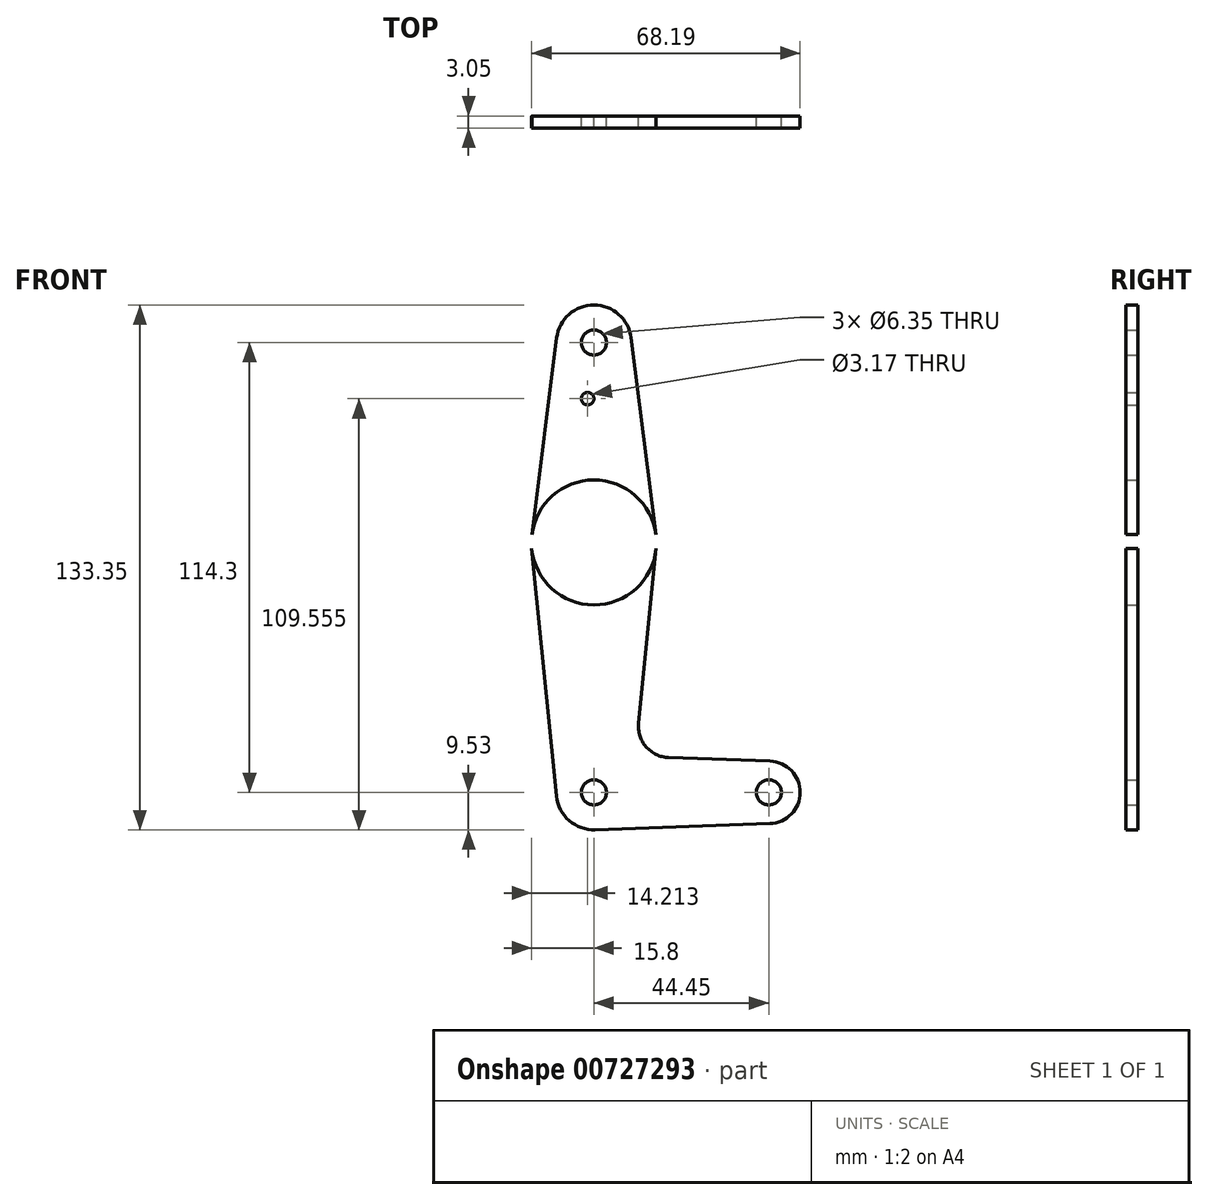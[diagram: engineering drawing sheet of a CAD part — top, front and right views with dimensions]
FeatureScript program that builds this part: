
annotation { "Feature Type Name" : "Feature", "Feature Type Description" : "" }
export const myFeature = defineFeature(function(context is Context, id is Id, definition is map)
    precondition{}
    {
        {
            var Q0;
            Q0=qCreatedBy(makeId("Front.planeOp"),FACE);
            var sketch = newSketch(context, id + "F0", { "sketchPlane" : qUnion([Q0])});
            skLineSegment(sketch, "E0", {"start": v(0, 0) * mm, "end": v(0, 50.8) * mm});
            skLineSegment(sketch, "E1", {"start": v(0, 50.8) * mm, "end": v(0, -63.5) * mm});
            skLineSegment(sketch, "E2", {"start": v(0, -63.5) * mm, "end": v(44.45, -63.5) * mm});
            skCircle(sketch, "E3", {"center": v(0, 50.8) * mm, "radius": 9.53 * mm});
            skCircle(sketch, "E4", {"center": v(0, 0) * mm, "radius": 15.88 * mm});
            skCircle(sketch, "E5", {"center": v(0, -63.5) * mm, "radius": 9.53 * mm});
            skCircle(sketch, "E6", {"center": v(44.45, -63.5) * mm, "radius": 7.94 * mm});
            skLineSegment(sketch, "E7", {"start": v(-9.45, 52) * mm, "end": v(-15.75, 1.98) * mm});
            skLineSegment(sketch, "E8", {"start": v(9.45, 52) * mm, "end": v(15.75, 1.98) * mm});
            skLineSegment(sketch, "E9", {"start": v(-15.8, -1.59) * mm, "end": v(-9.48, -64.45) * mm});
            skLineSegment(sketch, "E10", {"start": v(15.8, -1.59) * mm, "end": v(11.34, -45.9) * mm});
            skLineSegment(sketch, "E11", {"start": v(44.73, -55.57) * mm, "end": v(18.97, -54.65) * mm});
            skLineSegment(sketch, "E12", {"start": v(0.34, -73.02) * mm, "end": v(44.73, -71.43) * mm});
            skCircle(sketch, "E13", {"center": v(0, 50.8) * mm, "radius": 3.18 * mm});
            skCircle(sketch, "E14", {"center": v(0, 0) * mm, "radius": 3.18 * mm});
            skCircle(sketch, "E15", {"center": v(0, -63.5) * mm, "radius": 3.18 * mm});
            skCircle(sketch, "E16", {"center": v(44.45, -63.5) * mm, "radius": 3.18 * mm});
            skArc(sketch, "E17.filletArc", {"start": v(11.34, -45.9) * mm, "mid": v(13.26, -51.93) * mm, "end": v(18.97, -54.65) * mm});
            skCircle(sketch, "E18", {"center": v(-1.59, 36.53) * mm, "radius": 1.59 * mm});
            skSolve(sketch);
        }
        {
            var Q0;
            {var subQ0=sQuery(id+"F0.wireOp",EDGE,"E7");Q0=makeQuery(id+"F0.imprint","IMPRINT",FACE,{"disambiguationData":[TD([[makeQuery(id+"F0.imprint","IMPRINT",EDGE,{"derivedFrom":subQ0}),1.0]])]});}
            var Q1;
            {var subQ0=sQuery(id+"F0.wireOp",EDGE,"E8");Q1=makeQuery(id+"F0.imprint","IMPRINT",FACE,{"disambiguationData":[TD([[makeQuery(id+"F0.imprint","IMPRINT",EDGE,{"derivedFrom":subQ0}),-1.0]])]});}
            var Q2;
            Q2=makeQuery(id+"F0.imprint","IMPRINT",FACE,{"disambiguationData":[TD([[makeQuery(id+"F0.imprint","IMPRINT",EDGE,{"derivedFrom":sQuery(id+"F0.wireOp",EDGE,"E13")}),-1.0]])]});
            var Q3;
            {var subQ0=sQuery(id+"F0.wireOp",EDGE,"E4");var subQ2=sQuery(id+"F0.wireOp",EDGE,"E1");var subQ5=makeQuery(id+"F0.imprint","INTERSECT",VERTEX,{"disambiguationData":[OD(0.0)],"derivedFrom":[subQ2,subQ0]});Q3=makeQuery(id+"F0.imprint","IMPRINT",FACE,{"disambiguationData":[TD([[makeQuery(id+"F0.imprint","IMPRINT",EDGE,{"disambiguationData":[TD([[subQ5,-1.0]])],"derivedFrom":subQ2}),1.0]])]});}
            var Q4;
            {var subQ0=sQuery(id+"F0.wireOp",EDGE,"E10");Q4=makeQuery(id+"F0.imprint","IMPRINT",FACE,{"disambiguationData":[TD([[makeQuery(id+"F0.imprint","IMPRINT",EDGE,{"derivedFrom":subQ0}),-1.0]])]});}
            var Q5;
            {var subQ5=sQuery(id+"F0.wireOp",EDGE,"E9");Q5=makeQuery(id+"F0.imprint","IMPRINT",FACE,{"disambiguationData":[TD([[makeQuery(id+"F0.imprint","IMPRINT",EDGE,{"derivedFrom":subQ5}),1.0]])]});}
            var Q6;
            {var subQ0=sQuery(id+"F0.wireOp",EDGE,"E4");var subQ2=sQuery(id+"F0.wireOp",EDGE,"E1");var subQ3=makeQuery(id+"F0.imprint","INTERSECT",VERTEX,{"disambiguationData":[OD(0.0)],"derivedFrom":[subQ2,subQ0]});Q6=makeQuery(id+"F0.imprint","IMPRINT",FACE,{"disambiguationData":[TD([[makeQuery(id+"F0.imprint","IMPRINT",EDGE,{"disambiguationData":[TD([[subQ3,-1.0]])],"derivedFrom":subQ2}),-1.0]])]});}
            var Q7;
            {var subQ5=sQuery(id+"F0.wireOp",EDGE,"E12");Q7=makeQuery(id+"F0.imprint","IMPRINT",FACE,{"disambiguationData":[TD([[makeQuery(id+"F0.imprint","IMPRINT",EDGE,{"derivedFrom":subQ5}),1.0]])]});}
            var Q8;
            {var subQ0=sQuery(id+"F0.wireOp",EDGE,"E5");var subQ7=sQuery(id+"F0.wireOp",EDGE,"E1");var subQ8=makeQuery(id+"F0.imprint","INTERSECT",VERTEX,{"derivedFrom":[subQ7,subQ0]});Q8=makeQuery(id+"F0.imprint","IMPRINT",FACE,{"disambiguationData":[TD([[makeQuery(id+"F0.imprint","IMPRINT",EDGE,{"disambiguationData":[TD([[subQ8,-1.0]])],"derivedFrom":subQ7}),-1.0]])]});}
            var Q9;
            {var subQ0=sQuery(id+"F0.wireOp",EDGE,"E5");var subQ1=sQuery(id+"F0.wireOp",EDGE,"E1");var subQ2=makeQuery(id+"F0.imprint","INTERSECT",VERTEX,{"derivedFrom":[subQ1,subQ0]});Q9=makeQuery(id+"F0.imprint","IMPRINT",FACE,{"disambiguationData":[TD([[makeQuery(id+"F0.imprint","IMPRINT",EDGE,{"disambiguationData":[TD([[subQ2,-1.0]])],"derivedFrom":subQ1}),1.0]])]});}
            var Q10;
            Q10=makeQuery(id+"F0.imprint","IMPRINT",FACE,{"disambiguationData":[TD([[makeQuery(id+"F0.imprint","IMPRINT",EDGE,{"derivedFrom":sQuery(id+"F0.wireOp",EDGE,"E16")}),-1.0]])]});
            extrude(context, id + "F1", {"entities" : qUnion([Q0, Q1, Q2, Q3, Q4, Q5, Q6, Q7, Q8, Q9, Q10]), "depth" : 3.05 * mm, "offsetDistance" : 25.4 * mm});
        }
    });
